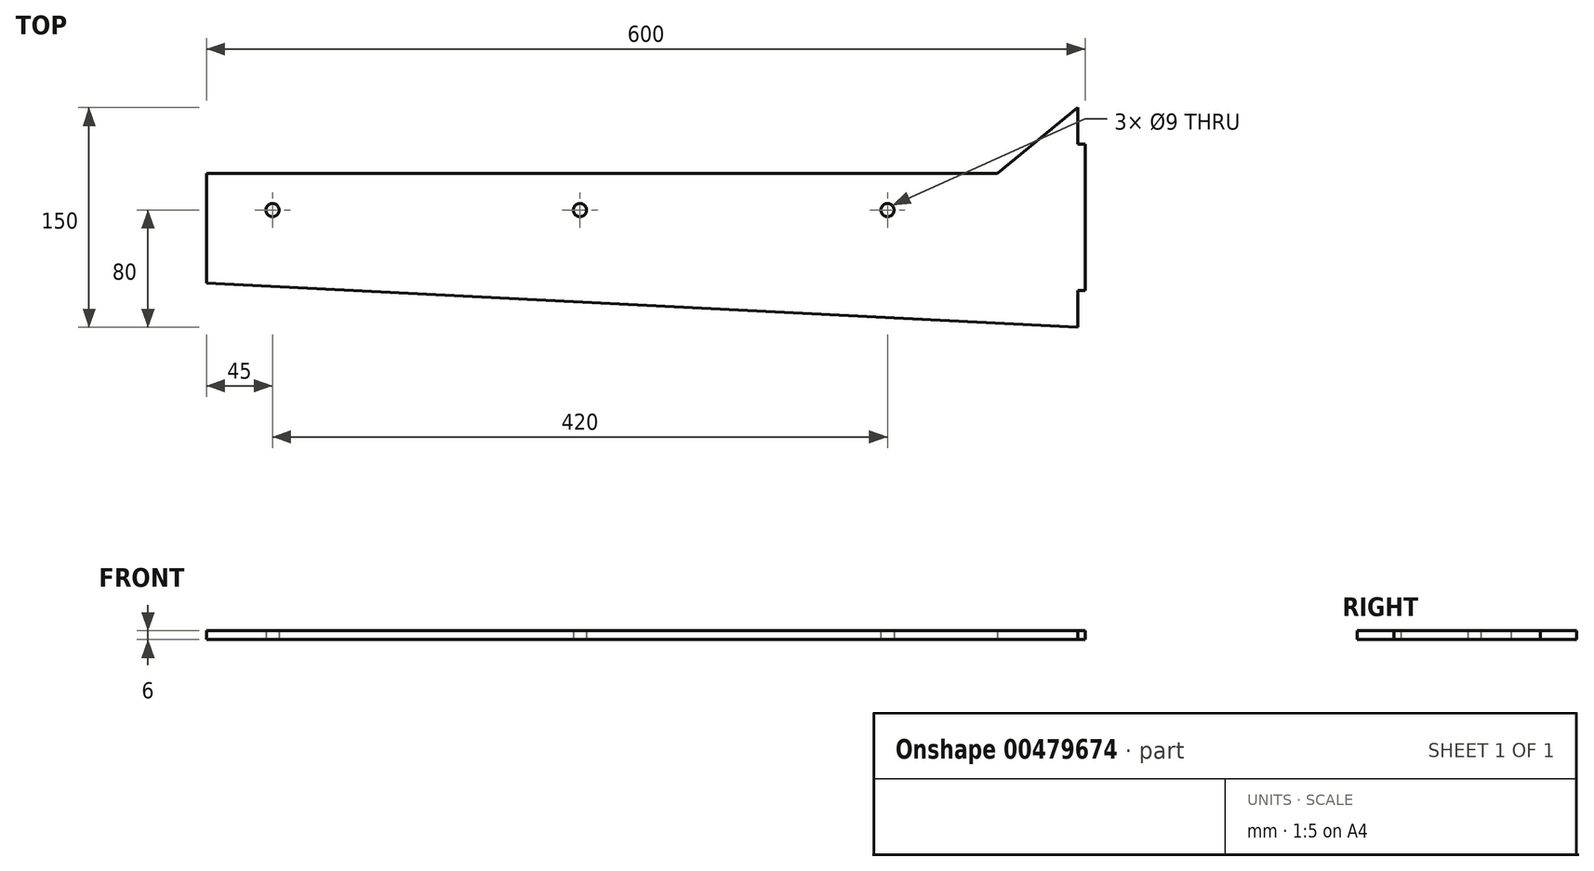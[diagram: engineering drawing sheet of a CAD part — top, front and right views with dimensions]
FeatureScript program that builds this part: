
annotation { "Feature Type Name" : "Feature", "Feature Type Description" : "" }
export const myFeature = defineFeature(function(context is Context, id is Id, definition is map)
    precondition{}
    {
        {
            var Q0;
            Q0=qCreatedBy(makeId("Top.planeOp"),FACE);
            var sketch = newSketch(context, id + "F0", { "sketchPlane" : qUnion([Q0])});
            skLineSegment(sketch, "E0", {"start": v(0, 0) * mm, "end": v(0, 75) * mm});
            skLineSegment(sketch, "E1", {"start": v(595, 95) * mm, "end": v(600, 95) * mm});
            skLineSegment(sketch, "E2", {"start": v(600, 95) * mm, "end": v(600, -5) * mm});
            skLineSegment(sketch, "E3", {"start": v(600, -5) * mm, "end": v(600, -5) * mm});
            skLineSegment(sketch, "E4", {"start": v(0, 75) * mm, "end": v(540, 75) * mm});
            skLineSegment(sketch, "E5", {"start": v(540, 75) * mm, "end": v(595, 120) * mm});
            skLineSegment(sketch, "E6", {"start": v(595, 120) * mm, "end": v(595, 95) * mm});
            skLineSegment(sketch, "E7", {"start": v(600, -5) * mm, "end": v(595, -5) * mm});
            skLineSegment(sketch, "E8", {"start": v(595, -5) * mm, "end": v(595, -30) * mm});
            skLineSegment(sketch, "E9", {"start": v(595, -30) * mm, "end": v(0, 0) * mm});
            skCircle(sketch, "E10", {"center": v(45, 50) * mm, "radius": 4.5 * mm});
            skCircle(sketch, "E11", {"center": v(255, 50) * mm, "radius": 4.5 * mm});
            skCircle(sketch, "E12", {"center": v(465, 50) * mm, "radius": 4.5 * mm});
            skSolve(sketch);
        }
        {
            var Q0;
            Q0 = qSketchRegion(id + "F0", true);
            extrude(context, id + "F1", {"entities" : qUnion([Q0]), "depth" : 6 * mm, "offsetDistance" : 25 * mm});
        }
    });
